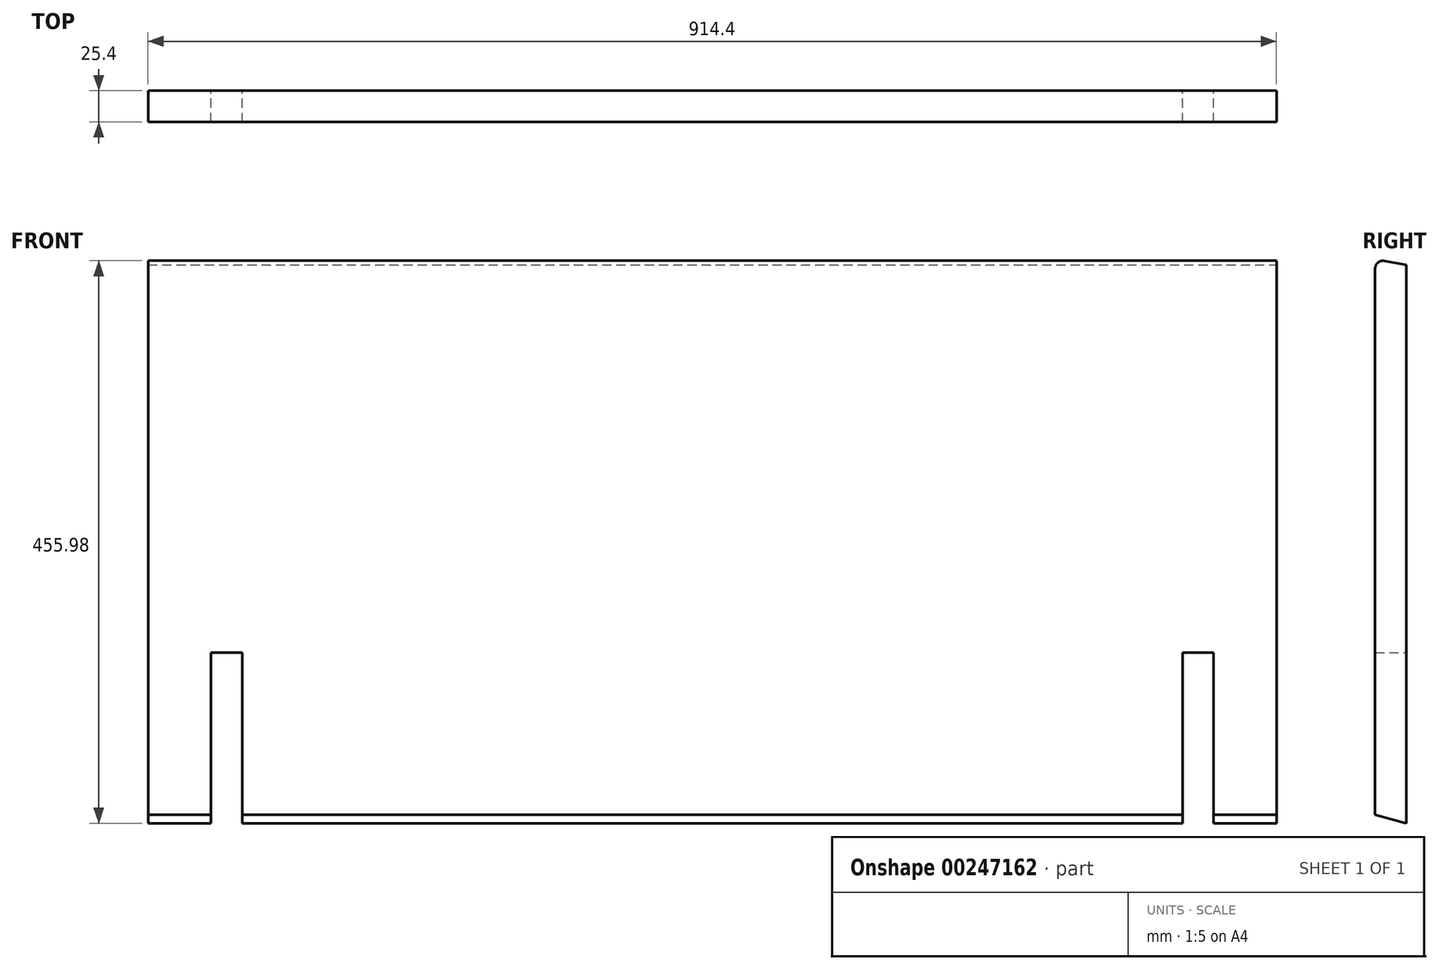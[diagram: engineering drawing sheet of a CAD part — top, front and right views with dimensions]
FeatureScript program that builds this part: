
annotation { "Feature Type Name" : "Feature", "Feature Type Description" : "" }
export const myFeature = defineFeature(function(context is Context, id is Id, definition is map)
    precondition{}
    {
        {
            var Q0;
            Q0=qCreatedBy(makeId("Front.planeOp"),FACE);
            var sketch = newSketch(context, id + "F0", { "sketchPlane" : qUnion([Q0])});
            skLineSegment(sketch, "E0.bottom", {"start": v(-431.4, 164.76) * mm, "end": v(483, 164.76) * mm});
            skLineSegment(sketch, "E0.top", {"start": v(-431.4, -292.44) * mm, "end": v(-380.6, -292.44) * mm});
            skLineSegment(sketch, "E0.left", {"start": v(-431.4, 164.76) * mm, "end": v(-431.4, -292.44) * mm});
            skLineSegment(sketch, "E0.right", {"start": v(483, 164.76) * mm, "end": v(483, -292.44) * mm});
            skLineSegment(sketch, "E1.top", {"start": v(-355.2, -154.17) * mm, "end": v(-380.6, -154.17) * mm});
            skLineSegment(sketch, "E1.left", {"start": v(-355.2, -292.44) * mm, "end": v(-355.2, -154.17) * mm});
            skLineSegment(sketch, "E1.right", {"start": v(-380.6, -292.44) * mm, "end": v(-380.6, -154.17) * mm});
            skPoint(sketch, "E2.oppositeSnap0", {"position": v(-367.9, -154.17) * mm});
            skLineSegment(sketch, "E2.top", {"start": v(432.2, -154.17) * mm, "end": v(406.8, -154.17) * mm});
            skLineSegment(sketch, "E2.left", {"start": v(432.2, -292.44) * mm, "end": v(432.2, -154.17) * mm});
            skLineSegment(sketch, "E2.right", {"start": v(406.8, -292.44) * mm, "end": v(406.8, -154.17) * mm});
            skLineSegment(sketch, "E3.trimOffspring", {"start": v(-355.2, -292.44) * mm, "end": v(406.8, -292.44) * mm});
            skLineSegment(sketch, "E4.trimOffspring", {"start": v(432.2, -292.44) * mm, "end": v(483, -292.44) * mm});
            skSolve(sketch);
        }
        {
            var Q0;
            Q0 = qSketchRegion(id + "F0", true);
            var Q1;
            Q1=makeQuery(id+"F0.imprint","IMPRINT",FACE,{"disambiguationData":[TD([[makeQuery(id+"F0.imprint","IMPRINT",EDGE,{"derivedFrom":sQuery(id+"F0.wireOp",EDGE,"E0.bottom")}),-1.0]])]});
            extrude(context, id + "F1", {"entities" : qUnion([Q0, Q1]), "depth" : 25.4 * mm});
        }
        {
            var Q0;
            Q0=makeQuery(id+"F1.opExtrude","SWEPT_FACE",FACE,{"disambiguationData":[OSD([sQuery(id+"F0.wireOp",EDGE,"E0.right")])]});
            var sketch = newSketch(context, id + "F2", { "sketchPlane" : qUnion([Q0])});
            skLineSegment(sketch, "E5", {"start": v(-25.4, 164.76) * mm, "end": v(0, 160.28) * mm});
            skLineSegment(sketch, "E6", {"start": v(0, 160.28) * mm, "end": v(0, 164.76) * mm});
            skLineSegment(sketch, "E7", {"start": v(0, 164.76) * mm, "end": v(-25.4, 164.76) * mm});
            skSolve(sketch);
        }
        {
            var Q0;
            Q0 = qSketchRegion(id + "F2", true);
            extrude(context, id + "F3", {"entities" : qUnion([Q0]), "operationType" : NewBodyOperationType.REMOVE, "oppositeDirection" : true, "depth" : 914.4 * mm});
        }
        {
            var Q0;
            Q0=makeQuery(id+"F3.boolean.opBoolean","COPY",EDGE,{"derivedFrom":makeQuery(id+"F3.opExtrude","SWEPT_EDGE",EDGE,{"disambiguationData":[OSD([sQuery(id+"F0.wireOp",EDGE,"E0.right"),sQuery(id+"F2.wireOp",EDGE,"E5"),sQuery(id+"F2.wireOp",EDGE,"E6")])]})});
            var Q1;
            Q1=makeQuery(id+"F3.boolean.opBoolean","MERGE",EDGE,{"derivedFrom":[makeQuery(id+"F1.opExtrude","CAP_EDGE",EDGE,{"disambiguationData":[OSD([sQuery(id+"F0.wireOp",EDGE,"E0.bottom")])],"isStart":false}),makeQuery(id+"F3.opExtrude","SWEPT_EDGE",EDGE,{"disambiguationData":[OSD([sQuery(id+"F0.wireOp",EDGE,"E0.right"),sQuery(id+"F2.wireOp",EDGE,"E5"),sQuery(id+"F2.wireOp",EDGE,"E7")])]})]});
            fillet(context, id + "F4", {"entities" : qUnion([Q0, Q1]), "radius" : 6.35 * mm, "tangentPropagation" : true, "allowEdgeOverflow" : false});
        }
        {
            var Q0;
            Q0=makeQuery(id+"F1.opExtrude","SWEPT_FACE",FACE,{"disambiguationData":[OSD([sQuery(id+"F0.wireOp",EDGE,"E0.right")])]});
            var sketch = newSketch(context, id + "F5", { "sketchPlane" : qUnion([Q0])});
            skLineSegment(sketch, "E8", {"start": v(0, -292.44) * mm, "end": v(-25.4, -285.64) * mm});
            skLineSegment(sketch, "E9", {"start": v(-25.4, -285.64) * mm, "end": v(-25.4, -292.44) * mm});
            skLineSegment(sketch, "E10", {"start": v(-25.4, -292.44) * mm, "end": v(0, -292.44) * mm});
            skSolve(sketch);
        }
        {
            var Q0;
            Q0=makeQuery(id+"F5.imprint","IMPRINT",FACE,{"disambiguationData":[TD([[makeQuery(id+"F5.imprint","IMPRINT",EDGE,{"derivedFrom":sQuery(id+"F5.wireOp",EDGE,"E8")}),1.0]])]});
            extrude(context, id + "F6", {"entities" : qUnion([Q0]), "operationType" : NewBodyOperationType.REMOVE, "endBound" : BoundingType.THROUGH_ALL, "oppositeDirection" : true, "depth" : 25.4 * mm});
        }
    });
